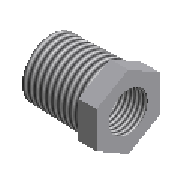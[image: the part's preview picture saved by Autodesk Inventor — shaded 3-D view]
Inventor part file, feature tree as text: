
AUTODESK INVENTOR PART (.ipt)
format: ipt  version: 2015 (Build 190159000, 159)  size: 201,728 bytes
history: native  units: mm (DEFAULTED — no unit token found)
features: other x8, sketch x2, revolve x1, extrude x1
ambient origin geometry x8: Origin, YZ Plane, XZ Plane, XY Plane, X Axis, Y Axis, Z Axis, Center Point
bodies: Body1 (feature_tree)
feature tree (12):
  revolve  "Revolve1"  [1 undecoded]
  extrude  "Extrude1"  Depth=5.0mm
  other  "Work Axis2"
  other  "Work Point3"
  other  "Work Axis3"
  other  "Work Point4"
  other  "Work Axis4"
  other  "Work Axis5"
  other  "Work Point5"
  other  "Work Point6"
  sketch  "Sketch1"  dims[d0=11.445mm d1=17.0mm]
  sketch  "Sketch2"  dims[d8=90.0deg d2=5.0mm d3=0.0mm d11=25.4mm d12=0.0mm d13=25.4mm d14=0.0mm d4=17.5mm d5=5.0mm d7=0.312398mm d9=12.4mm d10=5.833333mm d38=6.35mm d39=16.662mm]
note: 1 required parameter value undecoded (feature->parameter linkage not recoverable at this tier; creation-order binding heuristic only, values carry confidence <= 0.55)
